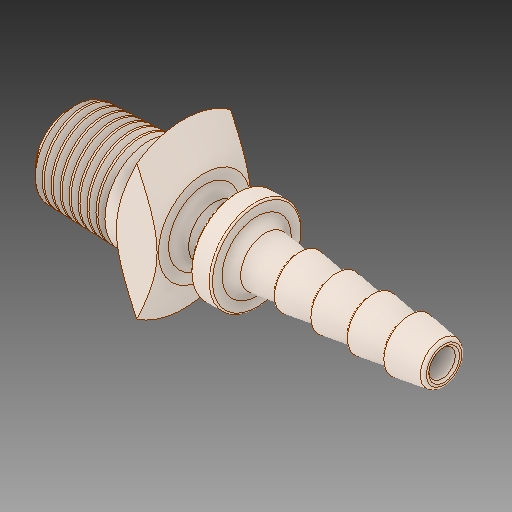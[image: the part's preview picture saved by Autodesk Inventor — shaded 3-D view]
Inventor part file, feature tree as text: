
AUTODESK INVENTOR PART (.ipt)
format: ipt  version: 2018 (Build 220112000, 112)  size: 736,768 bytes
history: native  units: in
note: dims shown in document units (in); Inventor stores cm internally (conversion verified against a paired STEP export)
features: fillet x1
ambient origin geometry x8: Origin, YZ Plane, XZ Plane, XY Plane, X Axis, Y Axis, Z Axis, Center Point
bodies: Solid1 (feature_tree)
feature tree (1):
  fillet  "Fillet3"  [1 undecoded]
note: 1 required parameter value undecoded (feature->parameter linkage not recoverable at this tier; creation-order binding heuristic only, values carry confidence <= 0.55)
